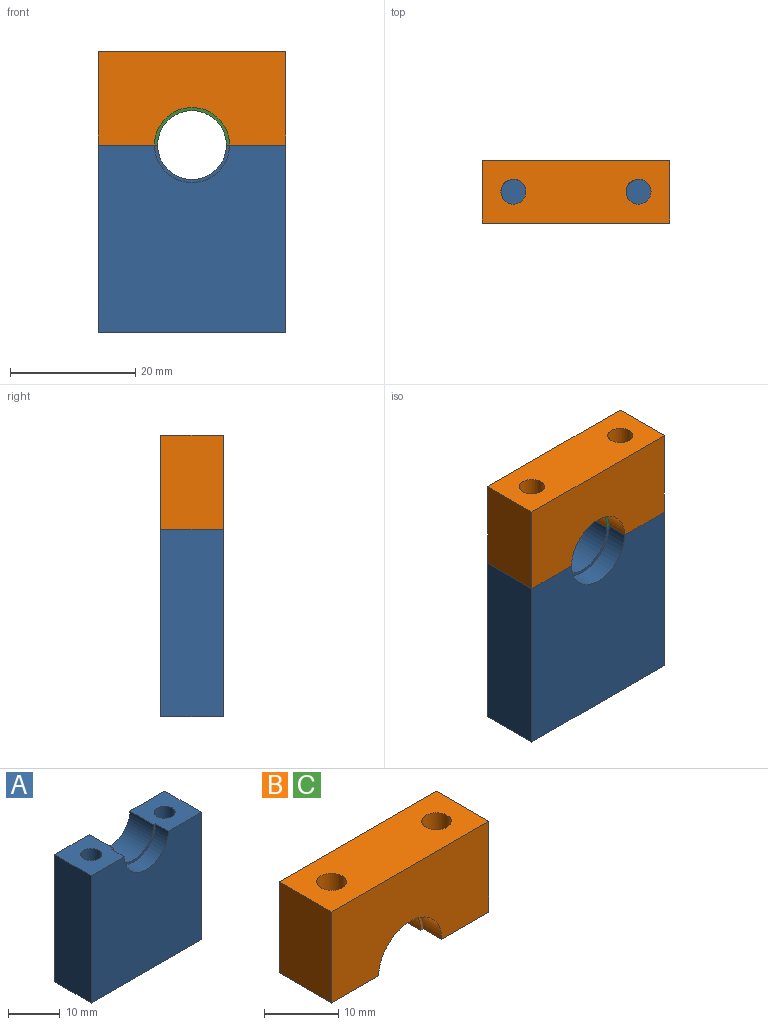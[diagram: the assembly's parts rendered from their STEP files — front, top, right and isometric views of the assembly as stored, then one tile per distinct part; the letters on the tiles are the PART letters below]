
ASSEMBLY  parts=3 mates=1
PART A: 18 faces, bbox 30x10x30 mm
  f0: plane 10x9.5mm, normal (0,0,1), area 80.7mm2, adj f1,f5,f6,f7,f8,f9,f12
  f1: plane 30x10mm, normal (1,0,0), area 300mm2, adj f0,f4,f5,f6
  f2: plane 10x9.5mm, normal (0,0,1), area 80.7mm2, adj f3,f5,f6,f7,f8,f9,f10
  f3: plane 30x10mm, normal (-1,0,0), area 300mm2, adj f2,f4,f5,f6
  f4: plane 30x10mm, normal (0,0,-1), area 274.9mm2, adj f1,f3,f5,f6,f14,f16
  f5: plane 30x30mm, normal (0,-1,0), area 843.5mm2, adj f0,f1,f2,f3,f4,f8
  f6: plane 30x30mm, normal (0,1,0), area 852.5mm2, adj f0,f1,f2,f3,f4,f9
  f7: plane 12x6mm, normal (0,-1,0), area 9mm2, adj f0,f2,f8,f9
  f8: cylinder r=6mm len=12mm, axis (0,-1,0), area 66mm2, adj f0,f2,f5,f7
  f9: cylinder r=5.5mm len=11mm, axis (0,-1,0), area 112.3mm2, adj f0,f2,f6,f7
  f10: cylinder r=2mm len=10mm, axis (0,0,1), area 125.7mm2, adj f2,f11
  f11: plane 4x4mm, normal (0,0,1), area 12.6mm2, adj f10
  f12: cylinder r=2mm len=10mm, axis (0,0,1), area 125.7mm2, adj f0,f13
  f13: plane 4x4mm, normal (0,0,1), area 12.6mm2, adj f12
  f14: cylinder r=2mm len=10mm, axis (0,0,-1), area 125.7mm2, adj f4,f15
  f15: plane 4x4mm, normal (0,0,-1), area 12.6mm2, adj f14
  f16: cylinder r=2mm len=10mm, axis (0,0,-1), area 125.7mm2, adj f4,f17
  f17: plane 4x4mm, normal (0,0,-1), area 12.6mm2, adj f16
PART B: 12 faces, bbox 30x10x15 mm
  f0: plane 10x9.5mm, normal (0,0,-1), area 80.7mm2, adj f1,f5,f6,f7,f8,f9,f11
  f1: plane 15x10mm, normal (1,0,0), area 150mm2, adj f0,f2,f5,f6
  f2: plane 30x10mm, normal (0,0,1), area 274.9mm2, adj f1,f3,f5,f6,f10,f11
  f3: plane 15x10mm, normal (-1,0,0), area 150mm2, adj f2,f4,f5,f6
  f4: plane 10x9.5mm, normal (0,0,-1), area 80.7mm2, adj f3,f5,f6,f7,f8,f9,f10
  f5: plane 30x15mm, normal (0,-1,0), area 393.5mm2, adj f0,f1,f2,f3,f4,f7
  f6: plane 30x15mm, normal (0,1,0), area 402.5mm2, adj f0,f1,f2,f3,f4,f9
  f7: cylinder r=6mm len=12mm, axis (0,-1,0), area 66mm2, adj f0,f4,f5,f8
  f8: plane 12x6mm, normal (0,-1,0), area 9mm2, adj f0,f4,f7,f9
  f9: cylinder r=5.5mm len=11mm, axis (0,-1,0), area 112.3mm2, adj f0,f4,f6,f8
  f10: cylinder r=2mm len=15mm, axis (0,0,1), area 188.5mm2, adj f2,f4
  f11: cylinder r=2mm len=15mm, axis (0,0,1), area 188.5mm2, adj f0,f2
PART C: same geometry as B
PLACE A t=(-3.08,-5.54,-7.65)mm
PLACE B t=(-3.08,-5.54,7.35)mm
PLACE C t=(-3.08,-5.54,7.35)mm
MATE fastened A.f10 <-> C.f10  axis (0,0,1) through (-28.08,-10.54,-7.65)mm
